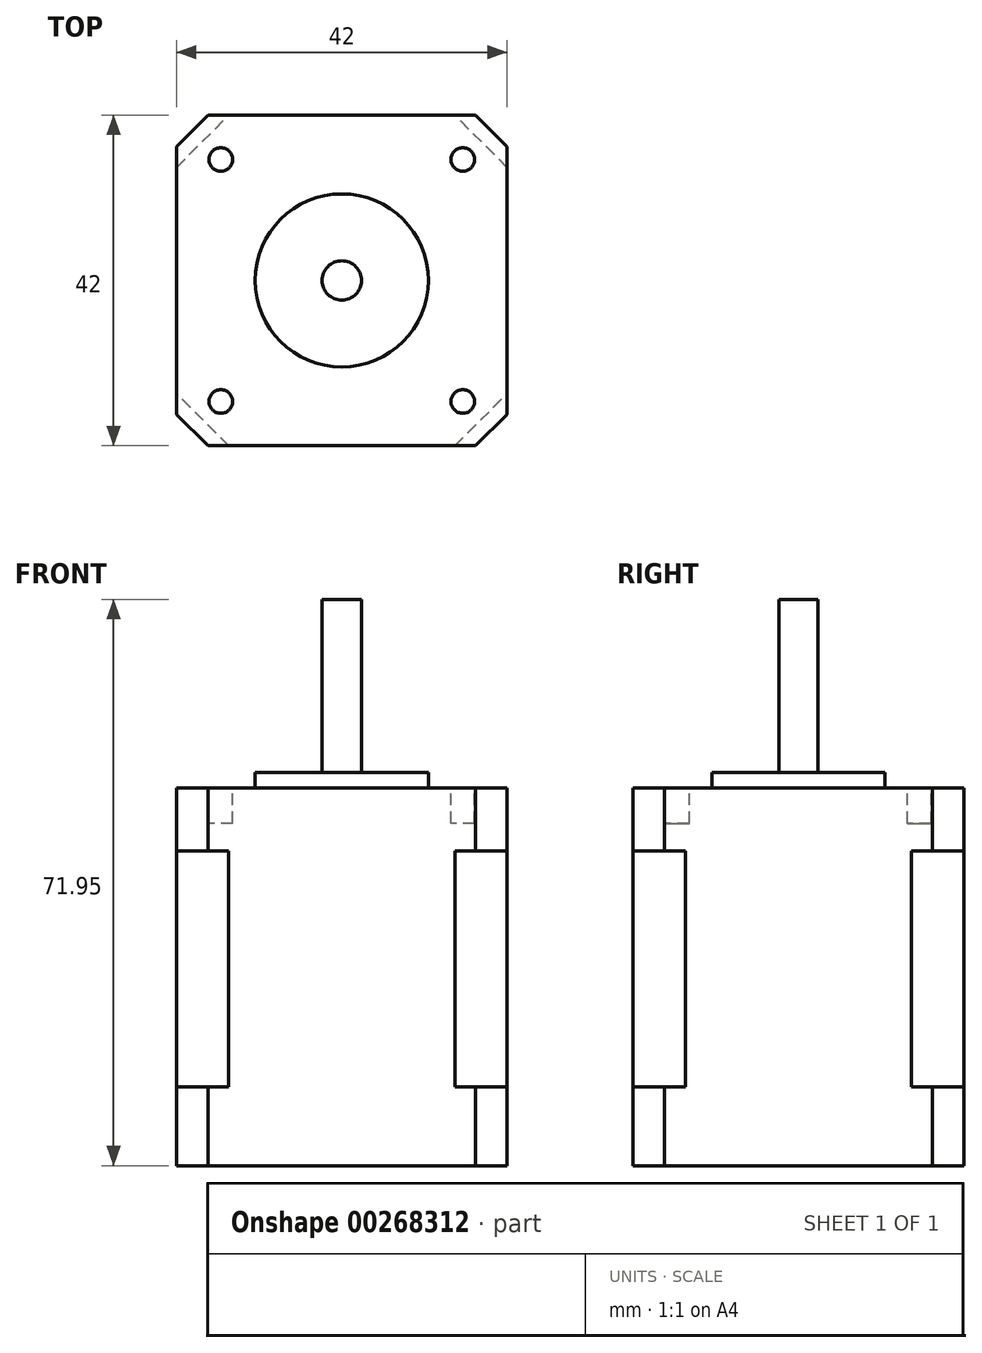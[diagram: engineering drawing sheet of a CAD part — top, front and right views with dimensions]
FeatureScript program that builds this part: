
annotation { "Feature Type Name" : "Feature", "Feature Type Description" : "" }
export const myFeature = defineFeature(function(context is Context, id is Id, definition is map)
    precondition{}
    {
        {
            var Q0;
            Q0=qCreatedBy(makeId("Top.planeOp"),FACE);
            var sketch = newSketch(context, id + "F0", { "sketchPlane" : qUnion([Q0])});
            skLineSegment(sketch, "E0.bottom", {"start": v(-21, -21) * mm, "end": v(21, -21) * mm});
            skLineSegment(sketch, "E0.top", {"start": v(-21, 21) * mm, "end": v(21, 21) * mm});
            skLineSegment(sketch, "E0.left", {"start": v(-21, -21) * mm, "end": v(-21, 21) * mm});
            skLineSegment(sketch, "E0.right", {"start": v(21, -21) * mm, "end": v(21, 21) * mm});
            skPoint(sketch, "E0.middle", {"position": v(0, 0) * mm});
            skCircle(sketch, "E1", {"center": v(0, 0) * mm, "radius": 11 * mm});
            skCircle(sketch, "E2", {"center": v(0, 0) * mm, "radius": 2.5 * mm});
            skCircle(sketch, "E3", {"center": v(-15.37, 15.37) * mm, "radius": 1.5 * mm});
            skCircle(sketch, "E4.MirrorC", {"center": v(15.37, 15.37) * mm, "radius": 1.5 * mm});
            skLineSegment(sketch, "E5.MirrorCS", {"start": v(21, 21) * mm, "end": v(-21, 21) * mm});
            skCircle(sketch, "E6.MirrorC", {"center": v(-15.37, -15.37) * mm, "radius": 1.5 * mm});
            skCircle(sketch, "E7.MirrorC", {"center": v(15.37, -15.37) * mm, "radius": 1.5 * mm});
            skSolve(sketch);
        }
        {
            var Q0;
            Q0=makeQuery(id+"F0.imprint","IMPRINT",FACE,{"disambiguationData":[TD([[makeQuery(id+"F0.imprint","IMPRINT",EDGE,{"derivedFrom":sQuery(id+"F0.wireOp",EDGE,"E0.bottom")}),1.0]])]});
            var Q1;
            Q1=makeQuery(id+"F0.imprint","IMPRINT",FACE,{"disambiguationData":[TD([[makeQuery(id+"F0.imprint","IMPRINT",EDGE,{"derivedFrom":sQuery(id+"F0.wireOp",EDGE,"E1")}),1.0]])]});
            var Q2;
            Q2=makeQuery(id+"F0.imprint","IMPRINT",FACE,{"disambiguationData":[TD([[makeQuery(id+"F0.imprint","IMPRINT",EDGE,{"derivedFrom":sQuery(id+"F0.wireOp",EDGE,"E2")}),1.0]])]});
            extrude(context, id + "F1", {"entities" : qUnion([Q0, Q1, Q2]), "oppositeDirection" : true, "depth" : 48 * mm});
        }
        {
            var Q0;
            Q0=makeQuery(id+"F0.imprint","IMPRINT",FACE,{"disambiguationData":[TD([[makeQuery(id+"F0.imprint","IMPRINT",EDGE,{"derivedFrom":sQuery(id+"F0.wireOp",EDGE,"E1")}),1.0]])]});
            var Q1;
            Q1=makeQuery(id+"F0.imprint","IMPRINT",FACE,{"disambiguationData":[TD([[makeQuery(id+"F0.imprint","IMPRINT",EDGE,{"derivedFrom":sQuery(id+"F0.wireOp",EDGE,"E2")}),1.0]])]});
            extrude(context, id + "F2", {"entities" : qUnion([Q0, Q1]), "operationType" : NewBodyOperationType.ADD, "depth" : 1.95 * mm});
        }
        {
            var Q0;
            Q0=makeQuery(id+"F2.opExtrude","CAP_FACE",FACE,{"disambiguationData":[OSD([sQuery(id+"F0.wireOp",EDGE,"E1")])],"isStart":false});
            cPlane(context, id + "F3", {"entities" : qUnion([Q0]), "cplaneType" : CPlaneType.OFFSET, "offset" : 22 * mm, "width" : 150 * mm, "height" : 150 * mm});
        }
        {
            var Q0;
            Q0=makeQuery(id+"F0.imprint","IMPRINT",FACE,{"disambiguationData":[TD([[makeQuery(id+"F0.imprint","IMPRINT",EDGE,{"derivedFrom":sQuery(id+"F0.wireOp",EDGE,"E2")}),1.0]])]});
            var Q1;
            Q1=qCreatedBy(id+"F3.planeOp",FACE);
            extrude(context, id + "F4", {"entities" : qUnion([Q0]), "operationType" : NewBodyOperationType.ADD, "endBound" : BoundingType.UP_TO_SURFACE, "endBoundEntityFace" : qUnion([Q1]), "depth" : 30 * mm});
        }
        {
            var Q0;
            Q0=makeQuery(id+"F0.imprint","IMPRINT",FACE,{"disambiguationData":[TD([[makeQuery(id+"F0.imprint","IMPRINT",EDGE,{"derivedFrom":sQuery(id+"F0.wireOp",EDGE,"E0.bottom")}),1.0]])]});
            var sketch = newSketch(context, id + "F5", { "sketchPlane" : qUnion([Q0])});
            skLineSegment(sketch, "E8.bottom", {"start": v(38, 0) * mm, "end": v(0, -38) * mm});
            skLineSegment(sketch, "E8.top", {"start": v(0, 38) * mm, "end": v(-38, 0) * mm});
            skLineSegment(sketch, "E8.left", {"start": v(38, 0) * mm, "end": v(0, 38) * mm});
            skLineSegment(sketch, "E8.right", {"start": v(0, -38) * mm, "end": v(-38, 0) * mm});
            skPoint(sketch, "E8.middle", {"position": v(0, 0) * mm});
            skSolve(sketch);
        }
        {
            var Q0;
            {var subQ0=sQuery(id+"F5.wireOp",EDGE,"E8.top");var subQ1=makeQuery(id+"F0.imprint","IMPRINT",EDGE,{"derivedFrom":sQuery(id+"F0.wireOp",EDGE,"E5.MirrorCS")});var subQ2=makeQuery(id+"F5.imprint","INTERSECT",VERTEX,{"derivedFrom":[subQ1,subQ0]});Q0=makeQuery(id+"F5.imprint","IMPRINT",FACE,{"disambiguationData":[TD([[makeQuery(id+"F5.imprint","IMPRINT",EDGE,{"disambiguationData":[TD([[subQ2,-1.0]])],"derivedFrom":subQ0}),-1.0]])]});}
            var Q1;
            {var subQ0=sQuery(id+"F5.wireOp",EDGE,"E8.right");var subQ1=makeQuery(id+"F0.imprint","IMPRINT",EDGE,{"derivedFrom":sQuery(id+"F0.wireOp",EDGE,"E0.bottom")});var subQ2=makeQuery(id+"F5.imprint","INTERSECT",VERTEX,{"derivedFrom":[subQ1,subQ0]});Q1=makeQuery(id+"F5.imprint","IMPRINT",FACE,{"disambiguationData":[TD([[makeQuery(id+"F5.imprint","IMPRINT",EDGE,{"disambiguationData":[TD([[subQ2,-1.0]])],"derivedFrom":subQ0}),1.0]])]});}
            var Q2;
            {var subQ0=sQuery(id+"F5.wireOp",EDGE,"E8.left");var subQ1=makeQuery(id+"F0.imprint","IMPRINT",EDGE,{"derivedFrom":sQuery(id+"F0.wireOp",EDGE,"E0.right")});var subQ2=makeQuery(id+"F5.imprint","INTERSECT",VERTEX,{"derivedFrom":[subQ1,subQ0]});Q2=makeQuery(id+"F5.imprint","IMPRINT",FACE,{"disambiguationData":[TD([[makeQuery(id+"F5.imprint","IMPRINT",EDGE,{"disambiguationData":[TD([[subQ2,-1.0]])],"derivedFrom":subQ0}),-1.0]])]});}
            var Q3;
            {var subQ0=sQuery(id+"F5.wireOp",EDGE,"E8.bottom");var subQ1=makeQuery(id+"F0.imprint","IMPRINT",EDGE,{"derivedFrom":sQuery(id+"F0.wireOp",EDGE,"E0.right")});var subQ2=makeQuery(id+"F5.imprint","INTERSECT",VERTEX,{"derivedFrom":[subQ1,subQ0]});Q3=makeQuery(id+"F5.imprint","IMPRINT",FACE,{"disambiguationData":[TD([[makeQuery(id+"F5.imprint","IMPRINT",EDGE,{"disambiguationData":[TD([[subQ2,-1.0]])],"derivedFrom":subQ0}),1.0]])]});}
            extrude(context, id + "F6", {"entities" : qUnion([Q0, Q1, Q2, Q3]), "operationType" : NewBodyOperationType.REMOVE, "endBound" : BoundingType.THROUGH_ALL, "oppositeDirection" : true, "depth" : 49.5 * mm});
        }
        {
            var Q0;
            Q0=makeQuery(id+"F1.opExtrude","CAP_FACE",FACE,{"disambiguationData":[OSD([sQuery(id+"F0.wireOp",EDGE,"E0.bottom"),sQuery(id+"F0.wireOp",EDGE,"E0.left"),sQuery(id+"F0.wireOp",EDGE,"E0.right"),sQuery(id+"F0.wireOp",EDGE,"E5.MirrorCS"),sQuery(id+"F0.wireOp",EDGE,"E4.MirrorC"),sQuery(id+"F0.wireOp",EDGE,"E3"),sQuery(id+"F0.wireOp",EDGE,"E6.MirrorC"),sQuery(id+"F0.wireOp",EDGE,"E7.MirrorC")])],"isStart":true});
            cPlane(context, id + "F7", {"entities" : qUnion([Q0]), "cplaneType" : CPlaneType.OFFSET, "offset" : 8 * mm, "oppositeDirection" : true, "width" : 150 * mm, "height" : 150 * mm});
        }
        {
            var Q0;
            Q0=qCreatedBy(id+"F7.planeOp",FACE);
            cPlane(context, id + "F8", {"entities" : qUnion([Q0]), "cplaneType" : CPlaneType.OFFSET, "offset" : 30 * mm, "oppositeDirection" : true, "width" : 150 * mm, "height" : 150 * mm});
        }
        {
            var Q0;
            Q0=qCreatedBy(id+"F8.planeOp",FACE);
            var sketch = newSketch(context, id + "F9", { "sketchPlane" : qUnion([Q0])});
            skLineSegment(sketch, "E9.bottom", {"start": v(14.36, -21) * mm, "end": v(21, -14.36) * mm});
            skLineSegment(sketch, "E9.top", {"start": v(-21, 14.36) * mm, "end": v(-14.36, 21) * mm});
            skLineSegment(sketch, "E9.left", {"start": v(-14.36, -21) * mm, "end": v(-21, -14.36) * mm});
            skLineSegment(sketch, "E9.right", {"start": v(21, 14.36) * mm, "end": v(14.36, 21) * mm});
            skPoint(sketch, "E9.middle", {"position": v(0, 0) * mm});
            skLineSegment(sketch, "E10.0.0", {"start": v(21, 17) * mm, "end": v(17, 21) * mm});
            skLineSegment(sketch, "E10.0.2", {"start": v(17, 21) * mm, "end": v(21, 17) * mm});
            skLineSegment(sketch, "E11.0.1", {"start": v(21, -17) * mm, "end": v(21, -14.36) * mm});
            skLineSegment(sketch, "E11.0.3", {"start": v(21, 17) * mm, "end": v(21, 14.36) * mm});
            skLineSegment(sketch, "E12.0.0", {"start": v(17, 21) * mm, "end": v(14.36, 21) * mm});
            skLineSegment(sketch, "E12.0.2", {"start": v(-17, 21) * mm, "end": v(-14.36, 21) * mm});
            skLineSegment(sketch, "E13.0.0", {"start": v(-17, 21) * mm, "end": v(-21, 17) * mm});
            skLineSegment(sketch, "E13.0.2", {"start": v(-21, 17) * mm, "end": v(-17, 21) * mm});
            skLineSegment(sketch, "E14.0.1", {"start": v(-21, 17) * mm, "end": v(-21, 14.36) * mm});
            skLineSegment(sketch, "E14.0.3", {"start": v(-21, -17) * mm, "end": v(-21, -14.36) * mm});
            skLineSegment(sketch, "E15.0.1", {"start": v(-17, -21) * mm, "end": v(-21, -17) * mm});
            skLineSegment(sketch, "E15.0.3", {"start": v(-21, -17) * mm, "end": v(-17, -21) * mm});
            skLineSegment(sketch, "E16.0.0", {"start": v(-17, -21) * mm, "end": v(-14.36, -21) * mm});
            skLineSegment(sketch, "E16.0.2", {"start": v(17, -21) * mm, "end": v(14.36, -21) * mm});
            skLineSegment(sketch, "E17.0.1", {"start": v(21, -17) * mm, "end": v(17, -21) * mm});
            skLineSegment(sketch, "E17.0.3", {"start": v(17, -21) * mm, "end": v(21, -17) * mm});
            skPoint(sketch, "E18.orphan", {"position": v(-35.36, 0) * mm});
            skLineSegment(sketch, "E19.trimOffspring", {"start": v(21, 14.36) * mm, "end": v(21, 17) * mm});
            skLineSegment(sketch, "E20.trimOffspring", {"start": v(14.36, 21) * mm, "end": v(17, 21) * mm});
            skLineSegment(sketch, "E21.trimOffspring", {"start": v(-14.36, -21) * mm, "end": v(-17, -21) * mm});
            skPoint(sketch, "E22.orphan", {"position": v(35.36, 0) * mm});
            skLineSegment(sketch, "E23.trimOffspring", {"start": v(21, -14.36) * mm, "end": v(21, -17) * mm});
            skLineSegment(sketch, "E24.trimOffspring", {"start": v(14.36, -21) * mm, "end": v(17, -21) * mm});
            skLineSegment(sketch, "E25.trimOffspring", {"start": v(-21, -14.36) * mm, "end": v(-21, -17) * mm});
            skLineSegment(sketch, "E26.trimOffspring", {"start": v(-14.36, 21) * mm, "end": v(-17, 21) * mm});
            skLineSegment(sketch, "E27.trimOffspring", {"start": v(-21, 14.36) * mm, "end": v(-21, 17) * mm});
            skSolve(sketch);
        }
        {
            var Q0;
            Q0 = qSketchRegion(id + "F9", true);
            var Q1;
            Q1=qCreatedBy(id+"F7.planeOp",FACE);
            extrude(context, id + "F10", {"entities" : qUnion([Q0]), "operationType" : NewBodyOperationType.REMOVE, "endBound" : BoundingType.UP_TO_SURFACE, "endBoundEntityFace" : qUnion([Q1]), "depth" : 25 * mm});
        }
        {
            var Q0;
            Q0=makeQuery(id+"F1.opExtrude","CAP_FACE",FACE,{"disambiguationData":[OSD([sQuery(id+"F0.wireOp",EDGE,"E0.bottom"),sQuery(id+"F0.wireOp",EDGE,"E0.left"),sQuery(id+"F0.wireOp",EDGE,"E0.right"),sQuery(id+"F0.wireOp",EDGE,"E5.MirrorCS"),sQuery(id+"F0.wireOp",EDGE,"E4.MirrorC"),sQuery(id+"F0.wireOp",EDGE,"E3"),sQuery(id+"F0.wireOp",EDGE,"E6.MirrorC"),sQuery(id+"F0.wireOp",EDGE,"E7.MirrorC")])],"isStart":true});
            cPlane(context, id + "F11", {"entities" : qUnion([Q0]), "cplaneType" : CPlaneType.OFFSET, "offset" : 4.5 * mm, "oppositeDirection" : true, "width" : 150 * mm, "height" : 150 * mm});
        }
        {
            var Q0;
            Q0=qCreatedBy(id+"F11.planeOp",FACE);
            var sketch = newSketch(context, id + "F12", { "sketchPlane" : qUnion([Q0])});
            skCircle(sketch, "E28.0", {"center": v(-15.37, 15.37) * mm, "radius": 1.5 * mm});
            skCircle(sketch, "E29.0", {"center": v(15.37, 15.37) * mm, "radius": 1.5 * mm});
            skCircle(sketch, "E30.0", {"center": v(15.37, -15.37) * mm, "radius": 1.5 * mm});
            skCircle(sketch, "E31.0", {"center": v(-15.37, -15.37) * mm, "radius": 1.5 * mm});
            skSolve(sketch);
        }
        {
            var Q0;
            Q0 = qSketchRegion(id + "F12", true);
            var Q1;
            Q1=makeQuery(id+"F1.opExtrude","CAP_FACE",FACE,{"disambiguationData":[OSD([sQuery(id+"F0.wireOp",EDGE,"E0.bottom"),sQuery(id+"F0.wireOp",EDGE,"E0.left"),sQuery(id+"F0.wireOp",EDGE,"E0.right"),sQuery(id+"F0.wireOp",EDGE,"E5.MirrorCS"),sQuery(id+"F0.wireOp",EDGE,"E4.MirrorC"),sQuery(id+"F0.wireOp",EDGE,"E3"),sQuery(id+"F0.wireOp",EDGE,"E6.MirrorC"),sQuery(id+"F0.wireOp",EDGE,"E7.MirrorC")])],"isStart":false});
            extrude(context, id + "F13", {"entities" : qUnion([Q0]), "operationType" : NewBodyOperationType.ADD, "endBound" : BoundingType.UP_TO_SURFACE, "oppositeDirection" : true, "endBoundEntityFace" : qUnion([Q1]), "depth" : 25 * mm});
        }
    });
